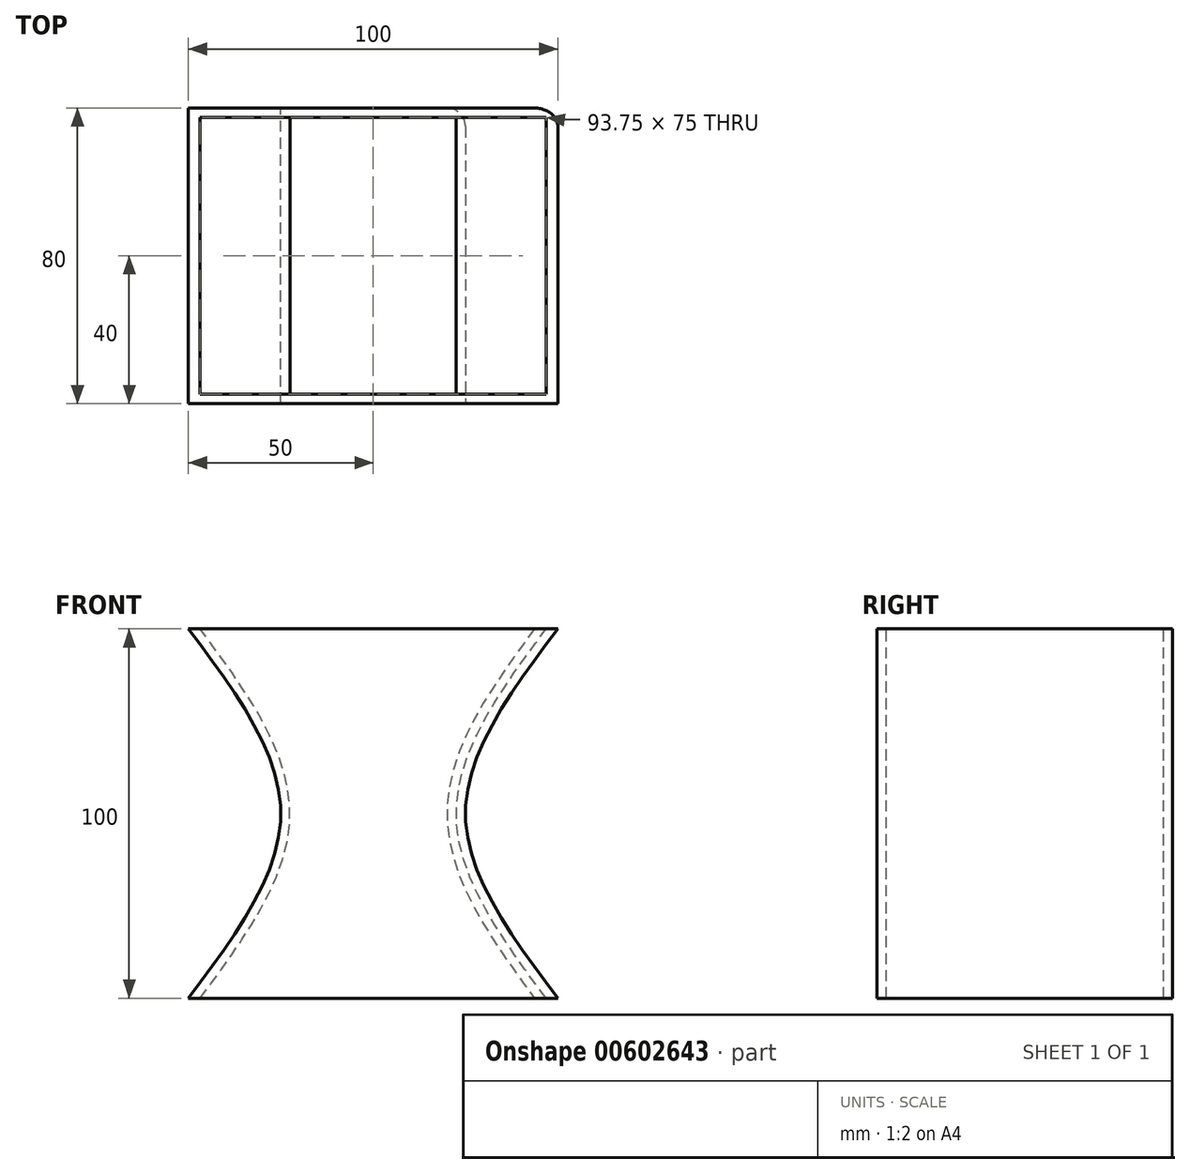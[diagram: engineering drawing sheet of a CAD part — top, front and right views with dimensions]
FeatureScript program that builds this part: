
annotation { "Feature Type Name" : "Feature", "Feature Type Description" : "" }
export const myFeature = defineFeature(function(context is Context, id is Id, definition is map)
    precondition{}
    {
        {
            var Q0;
            Q0=qCreatedBy(makeId("Top.planeOp"),FACE);
            var sketch = newSketch(context, id + "F0", { "sketchPlane" : qUnion([Q0])});
            skLineSegment(sketch, "E0.bottom", {"start": v(-50, 40) * mm, "end": v(50, 40) * mm});
            skLineSegment(sketch, "E0.top", {"start": v(-50, -40) * mm, "end": v(50, -40) * mm});
            skLineSegment(sketch, "E0.left", {"start": v(-50, 40) * mm, "end": v(-50, -40) * mm});
            skLineSegment(sketch, "E0.right", {"start": v(50, 40) * mm, "end": v(50, -40) * mm});
            skSolve(sketch);
        }
        {
            var Q0;
            Q0=qCreatedBy(makeId("Top.planeOp"),FACE);
            cPlane(context, id + "F1", {"entities" : qUnion([Q0]), "cplaneType" : CPlaneType.OFFSET, "offset" : 50 * mm, "width" : 150 * mm, "height" : 150 * mm});
        }
        {
            var Q0;
            Q0=qCreatedBy(id+"F1.planeOp",FACE);
            var sketch = newSketch(context, id + "F2", { "sketchPlane" : qUnion([Q0])});
            skLineSegment(sketch, "E1.bottom", {"start": v(25, -40) * mm, "end": v(-25, -40) * mm});
            skLineSegment(sketch, "E1.top", {"start": v(25, 40) * mm, "end": v(-25, 40) * mm});
            skLineSegment(sketch, "E1.left", {"start": v(25, -40) * mm, "end": v(25, 40) * mm});
            skLineSegment(sketch, "E1.right", {"start": v(-25, -40) * mm, "end": v(-25, 40) * mm});
            skSolve(sketch);
        }
        {
            var Q0;
            Q0=qCreatedBy(id+"F1.planeOp",FACE);
            cPlane(context, id + "F3", {"entities" : qUnion([Q0]), "cplaneType" : CPlaneType.OFFSET, "offset" : 50 * mm, "width" : 150 * mm, "height" : 150 * mm});
        }
        {
            var Q0;
            Q0=qCreatedBy(id+"F3.planeOp",FACE);
            var sketch = newSketch(context, id + "F4", { "sketchPlane" : qUnion([Q0])});
            skLineSegment(sketch, "E2.bottom", {"start": v(-50, 40) * mm, "end": v(50, 40) * mm});
            skLineSegment(sketch, "E2.top", {"start": v(-50, -40) * mm, "end": v(50, -40) * mm});
            skLineSegment(sketch, "E2.left", {"start": v(-50, 40) * mm, "end": v(-50, -40) * mm});
            skLineSegment(sketch, "E2.right", {"start": v(50, 40) * mm, "end": v(50, -40) * mm});
            skSolve(sketch);
        }
        {
            var Q0;
            Q0=makeQuery(id+"F0.imprint","IMPRINT",FACE,{"disambiguationData":[TD([[makeQuery(id+"F0.imprint","IMPRINT",EDGE,{"derivedFrom":sQuery(id+"F0.wireOp",EDGE,"E0.bottom")}),-1.0]])]});
            var Q1;
            Q1=makeQuery(id+"F2.imprint","IMPRINT",FACE,{"disambiguationData":[TD([[makeQuery(id+"F2.imprint","IMPRINT",EDGE,{"derivedFrom":sQuery(id+"F2.wireOp",EDGE,"E1.bottom")}),-1.0]])]});
            var Q2;
            Q2=makeQuery(id+"F4.imprint","IMPRINT",FACE,{"disambiguationData":[TD([[makeQuery(id+"F4.imprint","IMPRINT",EDGE,{"derivedFrom":sQuery(id+"F4.wireOp",EDGE,"E2.bottom")}),-1.0]])]});
            var Q3;
            Q3 = qConstructionFilter(qBodyType(qCreatedBy(id + "F0" ,EDGE), BodyType.WIRE), ConstructionObject.NO);
            var Q4;
            Q4 = qConstructionFilter(qBodyType(qCreatedBy(id + "F2" ,EDGE), BodyType.WIRE), ConstructionObject.NO);
            var Q5;
            Q5 = qConstructionFilter(qBodyType(qCreatedBy(id + "F4" ,EDGE), BodyType.WIRE), ConstructionObject.NO);
            loft(context, id + "F5", {"sheetProfilesArray" : [{ "sheetProfileEntities" : qUnion([Q0]) }, { "sheetProfileEntities" : qUnion([Q1]) }, { "sheetProfileEntities" : qUnion([Q2]) }], "wireProfilesArray" : [{ "wireProfileEntities" : qUnion([Q3]) }, { "wireProfileEntities" : qUnion([Q4]) }, { "wireProfileEntities" : qUnion([Q5]) }]});
        }
        {
            var Q0;
            Q0=makeQuery(id+"F5.opLoft","CAP_FACE",FACE,{"disambiguationData":[OSD([makeQuery(id+"F4.imprint","IMPRINT",FACE,{"disambiguationData":[TD([[makeQuery(id+"F4.imprint","IMPRINT",EDGE,{"derivedFrom":sQuery(id+"F4.wireOp",EDGE,"E2.bottom")}),-1.0]])]})])],"isStart":true});
            var Q1;
            Q1=makeQuery(id+"F5.opLoft","CAP_FACE",FACE,{"disambiguationData":[OSD([makeQuery(id+"F0.imprint","IMPRINT",FACE,{"disambiguationData":[TD([[makeQuery(id+"F0.imprint","IMPRINT",EDGE,{"derivedFrom":sQuery(id+"F0.wireOp",EDGE,"E0.bottom")}),-1.0]])]})])],"isStart":true});
            shell(context, id + "F6", {"entities" : qUnion([Q0, Q1]), "thickness" : 2.5 * mm});
        }
        {
            var Q0;
            Q0=makeQuery(id+"F5.opLoft","SWEPT_EDGE",EDGE,{"disambiguationData":[OSD([sQuery(id+"F0.wireOp",EDGE,"E0.bottom"),sQuery(id+"F0.wireOp",EDGE,"E0.right"),sQuery(id+"F2.wireOp",EDGE,"E1.top"),sQuery(id+"F2.wireOp",EDGE,"E1.left")])]});
            fillet(context, id + "F7", {"entities" : qUnion([Q0]), "radius" : 5 * mm, "tangentPropagation" : true, "allowEdgeOverflow" : false});
        }
    });
